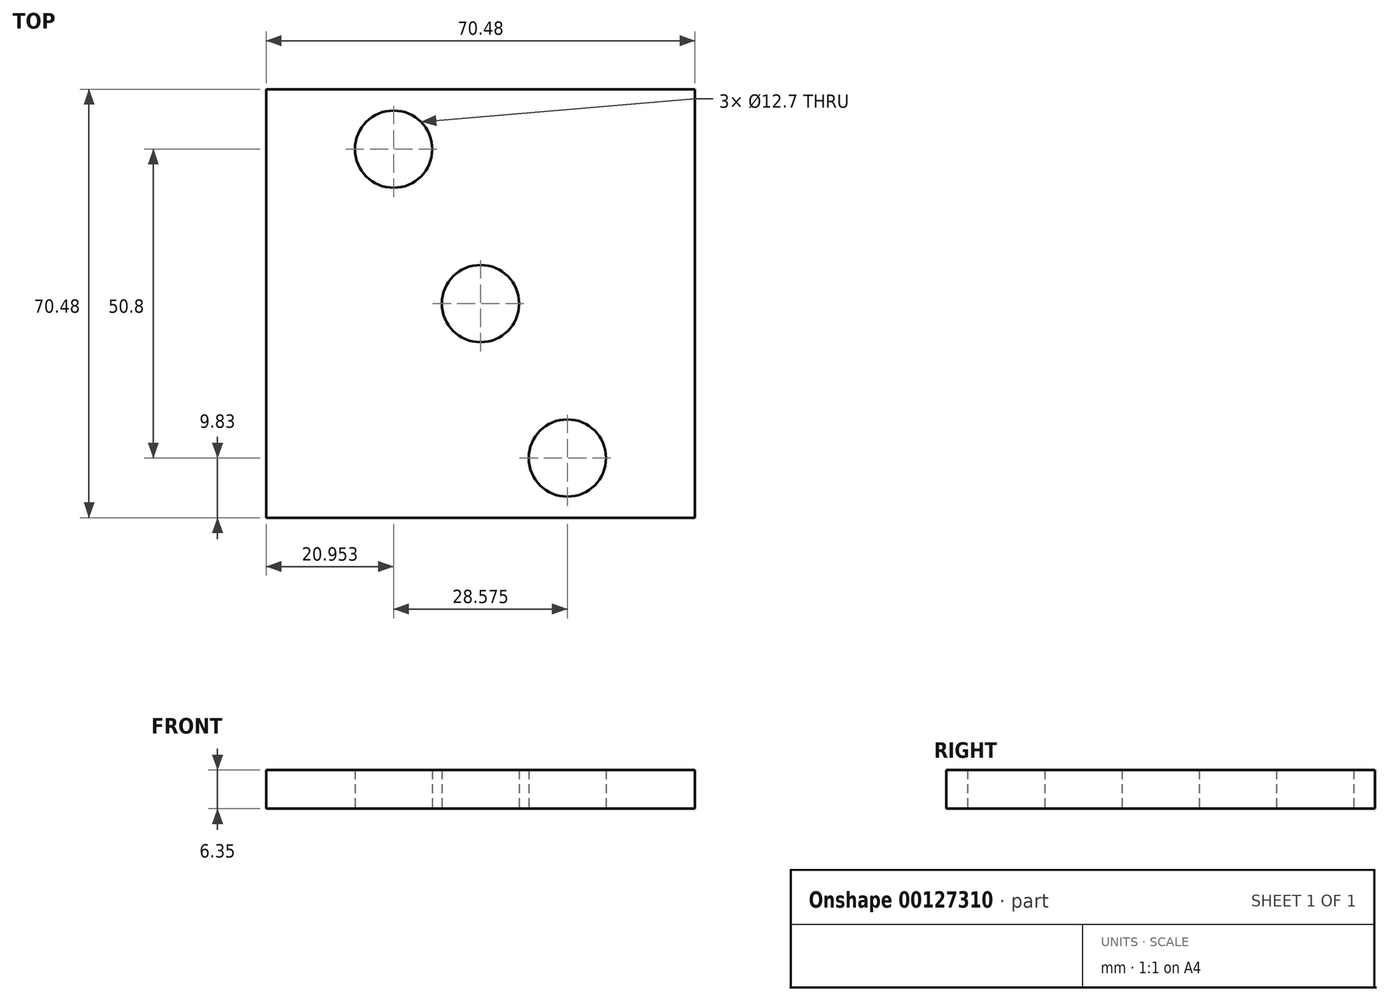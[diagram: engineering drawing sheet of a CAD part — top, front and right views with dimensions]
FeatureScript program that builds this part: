
annotation { "Feature Type Name" : "Feature", "Feature Type Description" : "" }
export const myFeature = defineFeature(function(context is Context, id is Id, definition is map)
    precondition{}
    {
        {
            var Q0;
            Q0=qCreatedBy(makeId("Top.planeOp"),FACE);
            var sketch = newSketch(context, id + "F0", { "sketchPlane" : qUnion([Q0])});
            skLineSegment(sketch, "E0.bottom", {"start": v(-35.24, 0) * mm, "end": v(-6.35, 0) * mm});
            skLineSegment(sketch, "E0.top", {"start": v(-35.24, 70.49) * mm, "end": v(35.24, 70.49) * mm});
            skLineSegment(sketch, "E0.left", {"start": v(-35.24, 0) * mm, "end": v(-35.24, 70.48) * mm});
            skLineSegment(sketch, "E0.right", {"start": v(35.24, 0) * mm, "end": v(35.24, 70.49) * mm});
            skPoint(sketch, "E1.centerSnap0", {"position": v(0, 0) * mm});
            skLineSegment(sketch, "E2.trimOffspring", {"start": v(6.35, 0) * mm, "end": v(35.24, 0) * mm});
            skLineSegment(sketch, "E3", {"start": v(-6.35, 0) * mm, "end": v(6.35, 0) * mm});
            skLineSegment(sketch, "E4.bottom", {"start": v(-35.24, 0) * mm, "end": v(35.24, 0) * mm});
            skLineSegment(sketch, "E4.left", {"start": v(-35.24, 0) * mm, "end": v(-35.24, 70.49) * mm});
            skPoint(sketch, "E5.centerSnap0", {"position": v(0, 70.49) * mm});
            skLineSegment(sketch, "E6", {"start": v(-22.54, 70.49) * mm, "end": v(-22.54, 0) * mm, "construction": true});
            skLineSegment(sketch, "E7", {"start": v(22.54, 70.49) * mm, "end": v(22.54, 0) * mm, "construction": true});
            skLineSegment(sketch, "E8.bottom", {"start": v(-14.29, 9.83) * mm, "end": v(14.29, 9.83) * mm, "construction": true});
            skLineSegment(sketch, "E8.top", {"start": v(-14.29, 60.63) * mm, "end": v(14.29, 60.63) * mm, "construction": true});
            skLineSegment(sketch, "E8.left", {"start": v(-14.29, 9.83) * mm, "end": v(-14.29, 60.63) * mm, "construction": true});
            skLineSegment(sketch, "E8.right", {"start": v(14.29, 9.83) * mm, "end": v(14.29, 60.63) * mm, "construction": true});
            skPoint(sketch, "E8.middle", {"position": v(0, 35.23) * mm});
            skCircle(sketch, "E9", {"center": v(-14.29, 60.63) * mm, "radius": 6.35 * mm});
            skCircle(sketch, "E10", {"center": v(14.29, 9.83) * mm, "radius": 6.35 * mm});
            skPoint(sketch, "E11.center.orphan", {"position": v(0, 57.79) * mm});
            skPoint(sketch, "E12.center.orphan", {"position": v(0, 12.7) * mm});
            skSolve(sketch);
        }
        {
            var Q0;
            Q0 = qSketchRegion(id + "F0", true);
            extrude(context, id + "F1", {"entities" : qUnion([Q0]), "depth" : 6.35 * mm});
        }
        {
            var Q0;
            Q0=makeQuery(id+"F1.opExtrude","CAP_FACE",FACE,{"disambiguationData":[OSD([sQuery(id+"F0.wireOp",EDGE,"E4.bottom"),sQuery(id+"F0.wireOp",EDGE,"E0.top"),sQuery(id+"F0.wireOp",EDGE,"E4.left"),sQuery(id+"F0.wireOp",EDGE,"E0.right"),sQuery(id+"F0.wireOp",EDGE,"E9"),sQuery(id+"F0.wireOp",EDGE,"96e83731-77c7-49e1-9d6c-d3304ee8419e"),sQuery(id+"F0.wireOp",EDGE,"E10"),sQuery(id+"F0.wireOp",EDGE,"38454114-c9a2-44da-9976-3e10870b0878")])],"isStart":true});
            var sketch = newSketch(context, id + "F2", { "sketchPlane" : qUnion([Q0])});
            skCircle(sketch, "E13", {"center": v(0, -35.23) * mm, "radius": 6.35 * mm});
            skPoint(sketch, "E13.centerSnap0", {"position": v(0, -70.49) * mm});
            skSolve(sketch);
        }
        {
            var Q0;
            Q0 = qSketchRegion(id + "F2", true);
            extrude(context, id + "F3", {"entities" : qUnion([Q0]), "operationType" : NewBodyOperationType.REMOVE, "endBound" : BoundingType.THROUGH_ALL, "oppositeDirection" : true, "depth" : 12.7 * mm});
        }
    });
